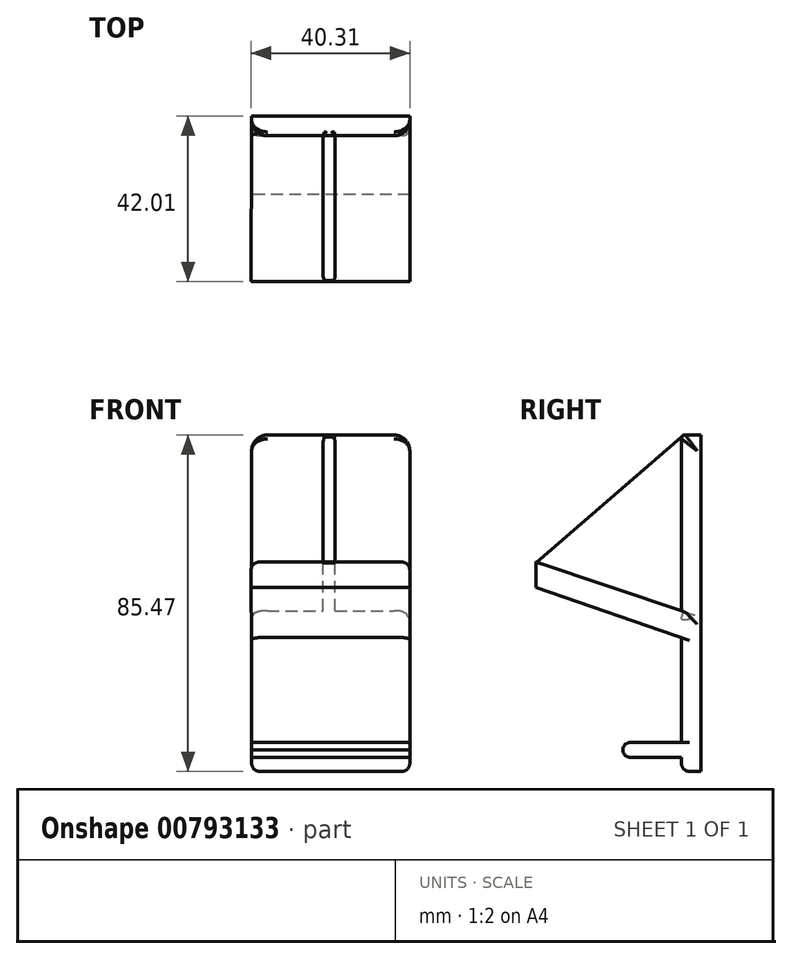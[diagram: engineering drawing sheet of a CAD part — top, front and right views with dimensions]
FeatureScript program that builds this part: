
annotation { "Feature Type Name" : "Feature", "Feature Type Description" : "" }
export const myFeature = defineFeature(function(context is Context, id is Id, definition is map)
    precondition{}
    {
        {
            var Q0;
            Q0=qCreatedBy(makeId("Front.planeOp"),FACE);
            var sketch = newSketch(context, id + "F0", { "sketchPlane" : qUnion([Q0])});
            skLineSegment(sketch, "E0.bottom", {"start": v(0, 0) * mm, "end": v(-40.17, 0) * mm});
            skLineSegment(sketch, "E0.top", {"start": v(0, 50.57) * mm, "end": v(-40.17, 50.57) * mm});
            skLineSegment(sketch, "E0.left", {"start": v(0, 0) * mm, "end": v(0, 50.57) * mm});
            skLineSegment(sketch, "E0.right", {"start": v(-40.17, 0) * mm, "end": v(-40.17, 50.57) * mm});
            skSolve(sketch);
        }
        {
            var Q0;
            Q0=makeQuery(id+"F0.imprint","IMPRINT",FACE,{"disambiguationData":[TD([[makeQuery(id+"F0.imprint","IMPRINT",EDGE,{"derivedFrom":sQuery(id+"F0.wireOp",EDGE,"E0.bottom")}),-1.0]])]});
            extrude(context, id + "F1", {"entities" : qUnion([Q0]), "depth" : 5 * mm, "offsetDistance" : 25 * mm});
        }
        {
            var Q0;
            Q0=makeQuery(id+"F1.opExtrude","CAP_FACE",FACE,{"disambiguationData":[OSD([sQuery(id+"F0.wireOp",EDGE,"E0.bottom"),sQuery(id+"F0.wireOp",EDGE,"E0.top"),sQuery(id+"F0.wireOp",EDGE,"E0.left"),sQuery(id+"F0.wireOp",EDGE,"E0.right")])],"isStart":false});
            var sketch = newSketch(context, id + "F2", { "sketchPlane" : qUnion([Q0])});
            skLineSegment(sketch, "E1.bottom", {"start": v(-40.17, 40.81) * mm, "end": v(0, 40.81) * mm});
            skLineSegment(sketch, "E1.top", {"start": v(-40.17, 33.98) * mm, "end": v(0, 33.98) * mm});
            skLineSegment(sketch, "E1.left", {"start": v(-40.17, 40.81) * mm, "end": v(-40.17, 33.98) * mm});
            skLineSegment(sketch, "E1.right", {"start": v(0, 40.81) * mm, "end": v(0, 33.98) * mm});
            skLineSegment(sketch, "E2.bottom", {"start": v(-40.17, 3.75) * mm, "end": v(0, 3.75) * mm});
            skLineSegment(sketch, "E2.top", {"start": v(-40.17, 7.39) * mm, "end": v(0, 7.39) * mm});
            skLineSegment(sketch, "E2.left", {"start": v(-40.17, 3.75) * mm, "end": v(-40.17, 7.39) * mm});
            skLineSegment(sketch, "E2.right", {"start": v(0, 3.75) * mm, "end": v(0, 7.39) * mm});
            skSolve(sketch);
        }
        {
            var Q0;
            {var subQ0=sQuery(id+"F0.wireOp",EDGE,"E0.left");var subQ1=sQuery(id+"F0.wireOp",EDGE,"E0.right");var subQ2=sQuery(id+"F0.wireOp",EDGE,"E0.bottom");Q0=makeQuery(id+"F9hGHmxZNpTLbHW_1.boolean.opBoolean","SPLIT",FACE,{"disambiguationData":[TD([makeQuery(id+"F1.opExtrude","SWEPT_FACE",FACE,{"disambiguationData":[OSD([subQ2])]})])],"derivedFrom":makeQuery(id+"F1.opExtrude","CAP_FACE",FACE,{"disambiguationData":[OSD([subQ2,sQuery(id+"F0.wireOp",EDGE,"E0.top"),subQ0,subQ1])],"isStart":false})});}
            var sketch = newSketch(context, id + "F3", { "sketchPlane" : qUnion([Q0])});
            skLineSegment(sketch, "E3.bottom", {"start": v(-40.17, 7.36) * mm, "end": v(0, 7.36) * mm});
            skLineSegment(sketch, "E3.top", {"start": v(-40.17, 3.54) * mm, "end": v(0, 3.54) * mm});
            skLineSegment(sketch, "E3.left", {"start": v(-40.17, 7.36) * mm, "end": v(-40.17, 3.54) * mm});
            skLineSegment(sketch, "E3.right", {"start": v(0, 7.36) * mm, "end": v(0, 3.54) * mm});
            skSolve(sketch);
        }
        {
            var Q0;
            Q0=makeQuery(id+"F3.imprint","IMPRINT",FACE,{"disambiguationData":[TD([[makeQuery(id+"F3.imprint","IMPRINT",EDGE,{"derivedFrom":sQuery(id+"F3.wireOp",EDGE,"E3.bottom")}),-1.0]])]});
            extrude(context, id + "F4", {"entities" : qUnion([Q0]), "operationType" : NewBodyOperationType.ADD, "depth" : 14.9 * mm, "offsetDistance" : 25 * mm});
        }
        {
            var Q0;
            Q0=makeQuery(id+"F1.opExtrude","SWEPT_FACE",FACE,{"disambiguationData":[OSD([sQuery(id+"F0.wireOp",EDGE,"E0.top")])]});
            extrude(context, id + "F5", {"entities" : qUnion([Q0]), "operationType" : NewBodyOperationType.ADD, "depth" : 15.1 * mm, "offsetDistance" : 25 * mm});
        }
        {
            var Q0;
            Q0=qCreatedBy(makeId("Front.planeOp"),FACE);
            cPlane(context, id + "F6", {"entities" : qUnion([Q0]), "cplaneType" : CPlaneType.OFFSET, "offset" : 42 * mm, "width" : 150 * mm, "height" : 150 * mm});
        }
        {
            var Q0;
            Q0=qCreatedBy(id+"F6.planeOp",FACE);
            var sketch = newSketch(context, id + "F7", { "sketchPlane" : qUnion([Q0])});
            skLineSegment(sketch, "E4.bottom", {"start": v(-40.31, 53.17) * mm, "end": v(0, 53.17) * mm});
            skLineSegment(sketch, "E4.top", {"start": v(-40.31, 46.74) * mm, "end": v(0, 46.74) * mm});
            skLineSegment(sketch, "E4.left", {"start": v(-40.31, 53.17) * mm, "end": v(-40.31, 46.74) * mm});
            skLineSegment(sketch, "E4.right", {"start": v(0, 53.17) * mm, "end": v(0, 46.74) * mm});
            skSolve(sketch);
        }
        {
            var Q1;
            Q1=makeQuery(id+"F2.imprint","IMPRINT",FACE,{"disambiguationData":[TD([[makeQuery(id+"F2.imprint","IMPRINT",EDGE,{"derivedFrom":sQuery(id+"F2.wireOp",EDGE,"E1.bottom")}),-1.0]])]});
            var Q2;
            Q2=makeQuery(id+"F7.imprint","IMPRINT",FACE,{"disambiguationData":[TD([[makeQuery(id+"F7.imprint","IMPRINT",EDGE,{"derivedFrom":sQuery(id+"F7.wireOp",EDGE,"E4.bottom")}),-1.0]])]});
            loft(context, id + "F8", {"operationType" : NewBodyOperationType.ADD, "sheetProfilesArray" : [{ "sheetProfileEntities" : qUnion([Q1]) }, { "sheetProfileEntities" : qUnion([Q2]) }]});
        }
        {
            var Q0;
            Q0=makeQuery(id+"F5.opExtrude","CAP_FACE",FACE,{"disambiguationData":[OSD([sQuery(id+"F0.wireOp",EDGE,"E0.top")])],"isStart":false});
            extrude(context, id + "F9", {"entities" : qUnion([Q0]), "operationType" : NewBodyOperationType.ADD, "depth" : 19.8 * mm, "offsetDistance" : 25 * mm});
        }
        {
            var Q0;
            Q0=qCreatedBy(makeId("Right.planeOp"),FACE);
            cPlane(context, id + "F10", {"entities" : qUnion([Q0]), "cplaneType" : CPlaneType.OFFSET, "offset" : 20 * mm, "oppositeDirection" : true, "width" : 150 * mm, "height" : 150 * mm});
        }
        {
            var Q0;
            Q0=qCreatedBy(id+"F10.planeOp",FACE);
            var sketch = newSketch(context, id + "F11", { "sketchPlane" : qUnion([Q0])});
            skLineSegment(sketch, "E5", {"start": v(-42.01, 52.93) * mm, "end": v(-4.9, 85.1) * mm});
            skLineSegment(sketch, "E6", {"start": v(-4.9, 85.1) * mm, "end": v(-4.9, 39.07) * mm});
            skLineSegment(sketch, "E7", {"start": v(-4.9, 39.07) * mm, "end": v(-42.01, 52.93) * mm});
            skSolve(sketch);
        }
        {
            var Q0;
            Q0=makeQuery(id+"F11.imprint","IMPRINT",FACE,{"disambiguationData":[TD([[makeQuery(id+"F11.imprint","IMPRINT",EDGE,{"derivedFrom":sQuery(id+"F11.wireOp",EDGE,"E5")}),-1.0]])]});
            extrude(context, id + "F12", {"entities" : qUnion([Q0]), "operationType" : NewBodyOperationType.ADD, "depth" : 1 * mm, "offsetDistance" : 25 * mm, "hasSecondDirection" : true, "secondDirectionOppositeDirection" : true, "secondDirectionDepth" : 2 * mm});
        }
        {
            var Q0;
            {var subQ0=sQuery(id+"F0.wireOp",EDGE,"E0.top");var subQ1=makeQuery(id+"F1.opExtrude","CAP_EDGE",EDGE,{"disambiguationData":[OSD([subQ0])],"isStart":false});var subQ4=sQuery(id+"F11.wireOp",EDGE,"E5");Q0=makeQuery(id+"F12.boolean.opBoolean","SPLIT",EDGE,{"disambiguationData":[TD([makeQuery(id+"F5.opExtrude","SWEPT_FACE",FACE,{"disambiguationData":[OSD([subQ0]),TDD([subQ1])]})])],"derivedFrom":makeQuery(id+"F12.opExtrude","CAP_EDGE",EDGE,{"disambiguationData":[OSD([subQ4])],"isStart":true})});}
            var Q1;
            {var subQ0=sQuery(id+"F0.wireOp",EDGE,"E0.top");var subQ1=makeQuery(id+"F1.opExtrude","CAP_EDGE",EDGE,{"disambiguationData":[OSD([subQ0])],"isStart":false});var subQ4=sQuery(id+"F11.wireOp",EDGE,"E5");Q1=makeQuery(id+"F12.boolean.opBoolean","SPLIT",EDGE,{"disambiguationData":[TD([makeQuery(id+"F5.opExtrude","SWEPT_FACE",FACE,{"disambiguationData":[OSD([subQ0]),TDD([subQ1])]})])],"derivedFrom":makeQuery(id+"F12.opExtrude","CAP_EDGE",EDGE,{"disambiguationData":[OSD([subQ4])],"isStart":false})});}
            fillet(context, id + "F13", {"entities" : qUnion([Q0, Q1]), "radius" : 1 * mm, "tangentPropagation" : true, "allowEdgeOverflow" : false});
        }
        {
            var Q0;
            {var subQ0=sQuery(id+"F0.wireOp",EDGE,"E0.top");Q0=makeQuery(id+"F9.opExtrude","CAP_EDGE",EDGE,{"disambiguationData":[OSD([subQ0]),TDD([makeQuery(id+"F5.opExtrude","CAP_EDGE",EDGE,{"disambiguationData":[OSD([subQ0]),TDD([makeQuery(id+"F1.opExtrude","CAP_EDGE",EDGE,{"disambiguationData":[OSD([subQ0])],"isStart":false})])],"isStart":false})])],"isStart":false});}
            fillet(context, id + "F14", {"entities" : qUnion([Q0]), "radius" : 1 * mm, "tangentPropagation" : true, "allowEdgeOverflow" : false});
        }
        {
            var Q0;
            {var subQ0=sQuery(id+"F0.wireOp",EDGE,"E0.left");var subQ1=sQuery(id+"F0.wireOp",EDGE,"E0.top");var subQ2=makeQuery(id+"F1.opExtrude","CAP_VERTEX",VERTEX,{"disambiguationData":[OSD([subQ1,subQ0])],"isStart":false});Q0=makeQuery(id+"F9.boolean.opBoolean","MERGE",EDGE,{"derivedFrom":[makeQuery(id+"F8.boolean.opBoolean","SPLIT",EDGE,{"disambiguationData":[TD([makeQuery(id+"F5.opExtrude","CAP_FACE",FACE,{"disambiguationData":[OSD([subQ1])],"isStart":false})])],"derivedFrom":makeQuery(id+"F5.boolean.opBoolean","MERGE",EDGE,{"derivedFrom":[makeQuery(id+"F4.boolean.opBoolean","SPLIT",EDGE,{"disambiguationData":[TD([makeQuery(id+"F1.opExtrude","SWEPT_FACE",FACE,{"disambiguationData":[OSD([subQ1])]})])],"derivedFrom":makeQuery(id+"F1.opExtrude","CAP_EDGE",EDGE,{"disambiguationData":[OSD([subQ0])],"isStart":false})}),makeQuery(id+"F5.opExtrude","SWEPT_EDGE",EDGE,{"disambiguationData":[OSD([subQ1,subQ0]),TDD([subQ2])]})]})}),makeQuery(id+"F9.opExtrude","SWEPT_EDGE",EDGE,{"disambiguationData":[OSD([subQ1,subQ0]),TDD([makeQuery(id+"F5.opExtrude","CAP_VERTEX",VERTEX,{"disambiguationData":[OSD([subQ1,subQ0]),TDD([subQ2])],"isStart":false})])]})]});}
            var Q1;
            {var subQ0=sQuery(id+"F0.wireOp",EDGE,"E0.right");var subQ1=sQuery(id+"F0.wireOp",EDGE,"E0.top");var subQ2=makeQuery(id+"F1.opExtrude","CAP_VERTEX",VERTEX,{"disambiguationData":[OSD([subQ1,subQ0])],"isStart":false});Q1=makeQuery(id+"F9.boolean.opBoolean","MERGE",EDGE,{"derivedFrom":[makeQuery(id+"F8.boolean.opBoolean","SPLIT",EDGE,{"disambiguationData":[TD([makeQuery(id+"F5.opExtrude","CAP_FACE",FACE,{"disambiguationData":[OSD([subQ1])],"isStart":false})])],"derivedFrom":makeQuery(id+"F5.boolean.opBoolean","MERGE",EDGE,{"derivedFrom":[makeQuery(id+"F4.boolean.opBoolean","SPLIT",EDGE,{"disambiguationData":[TD([makeQuery(id+"F1.opExtrude","SWEPT_FACE",FACE,{"disambiguationData":[OSD([subQ1])]})])],"derivedFrom":makeQuery(id+"F1.opExtrude","CAP_EDGE",EDGE,{"disambiguationData":[OSD([subQ0])],"isStart":false})}),makeQuery(id+"F5.opExtrude","SWEPT_EDGE",EDGE,{"disambiguationData":[OSD([subQ1,subQ0]),TDD([subQ2])]})]})}),makeQuery(id+"F9.opExtrude","SWEPT_EDGE",EDGE,{"disambiguationData":[OSD([subQ1,subQ0]),TDD([makeQuery(id+"F5.opExtrude","CAP_VERTEX",VERTEX,{"disambiguationData":[OSD([subQ1,subQ0]),TDD([subQ2])],"isStart":false})])]})]});}
            fillet(context, id + "F15", {"entities" : qUnion([Q0, Q1]), "radius" : 4 * mm, "tangentPropagation" : true, "allowEdgeOverflow" : false});
        }
        {
            var Q0;
            Q0=makeQuery(id+"F4.opExtrude","CAP_EDGE",EDGE,{"disambiguationData":[OSD([sQuery(id+"F3.wireOp",EDGE,"E3.top")])],"isStart":false});
            var Q1;
            Q1=makeQuery(id+"F4.opExtrude","CAP_EDGE",EDGE,{"disambiguationData":[OSD([sQuery(id+"F3.wireOp",EDGE,"E3.bottom")])],"isStart":false});
            var Q2;
            Q2=makeQuery(id+"F8.opLoft","SWEPT_EDGE",EDGE,{"disambiguationData":[OSD([sQuery(id+"F0.wireOp",EDGE,"E0.left"),sQuery(id+"F2.wireOp",EDGE,"E1.bottom"),sQuery(id+"F2.wireOp",EDGE,"E1.right"),sQuery(id+"F7.wireOp",EDGE,"E4.bottom"),sQuery(id+"F7.wireOp",EDGE,"E4.right")])]});
            var Q3;
            Q3=makeQuery(id+"F8.opLoft","SWEPT_EDGE",EDGE,{"disambiguationData":[OSD([sQuery(id+"F0.wireOp",EDGE,"E0.right"),sQuery(id+"F2.wireOp",EDGE,"E1.bottom"),sQuery(id+"F2.wireOp",EDGE,"E1.left"),sQuery(id+"F7.wireOp",EDGE,"E4.bottom"),sQuery(id+"F7.wireOp",EDGE,"E4.left")])]});
            var Q4;
            {var subQ1=makeQuery(id+"F4.opExtrude","SWEPT_FACE",FACE,{"disambiguationData":[OSD([sQuery(id+"F3.wireOp",EDGE,"E3.bottom")])]});var subQ2=sQuery(id+"F0.wireOp",EDGE,"E0.top");var subQ3=sQuery(id+"F0.wireOp",EDGE,"E0.left");Q4=makeQuery(id+"F8.boolean.opBoolean","SPLIT",EDGE,{"disambiguationData":[TD([subQ1])],"derivedFrom":makeQuery(id+"F5.boolean.opBoolean","MERGE",EDGE,{"derivedFrom":[makeQuery(id+"F4.boolean.opBoolean","SPLIT",EDGE,{"disambiguationData":[TD([makeQuery(id+"F1.opExtrude","SWEPT_FACE",FACE,{"disambiguationData":[OSD([subQ2])]})])],"derivedFrom":makeQuery(id+"F1.opExtrude","CAP_EDGE",EDGE,{"disambiguationData":[OSD([subQ3])],"isStart":false})}),makeQuery(id+"F5.opExtrude","SWEPT_EDGE",EDGE,{"disambiguationData":[OSD([subQ2,subQ3]),TDD([makeQuery(id+"F1.opExtrude","CAP_VERTEX",VERTEX,{"disambiguationData":[OSD([subQ2,subQ3])],"isStart":false})])]})]})});}
            var Q5;
            {var subQ1=sQuery(id+"F0.wireOp",EDGE,"E0.right");var subQ3=sQuery(id+"F0.wireOp",EDGE,"E0.top");var subQ5=makeQuery(id+"F4.opExtrude","SWEPT_FACE",FACE,{"disambiguationData":[OSD([sQuery(id+"F3.wireOp",EDGE,"E3.bottom")])]});Q5=makeQuery(id+"F8.boolean.opBoolean","SPLIT",EDGE,{"disambiguationData":[TD([subQ5])],"derivedFrom":makeQuery(id+"F5.boolean.opBoolean","MERGE",EDGE,{"derivedFrom":[makeQuery(id+"F4.boolean.opBoolean","SPLIT",EDGE,{"disambiguationData":[TD([makeQuery(id+"F1.opExtrude","SWEPT_FACE",FACE,{"disambiguationData":[OSD([subQ3])]})])],"derivedFrom":makeQuery(id+"F1.opExtrude","CAP_EDGE",EDGE,{"disambiguationData":[OSD([subQ1])],"isStart":false})}),makeQuery(id+"F5.opExtrude","SWEPT_EDGE",EDGE,{"disambiguationData":[OSD([subQ3,subQ1]),TDD([makeQuery(id+"F1.opExtrude","CAP_VERTEX",VERTEX,{"disambiguationData":[OSD([subQ3,subQ1])],"isStart":false})])]})]})});}
            var Q6;
            Q6=makeQuery(id+"F1.opExtrude","CAP_EDGE",EDGE,{"disambiguationData":[OSD([sQuery(id+"F0.wireOp",EDGE,"E0.bottom")])],"isStart":false});
            var Q7;
            Q7=makeQuery(id+"F1.opExtrude","SWEPT_EDGE",EDGE,{"disambiguationData":[OSD([sQuery(id+"F0.wireOp",EDGE,"E0.bottom"),sQuery(id+"F0.wireOp",EDGE,"E0.right")])]});
            var Q8;
            Q8=makeQuery(id+"F1.opExtrude","SWEPT_EDGE",EDGE,{"disambiguationData":[OSD([sQuery(id+"F0.wireOp",EDGE,"E0.bottom"),sQuery(id+"F0.wireOp",EDGE,"E0.left")])]});
            fillet(context, id + "F16", {"entities" : qUnion([Q0, Q1, Q2, Q3, Q4, Q5, Q6, Q7, Q8]), "radius" : 2 * mm, "tangentPropagation" : true, "allowEdgeOverflow" : false});
        }
    });
